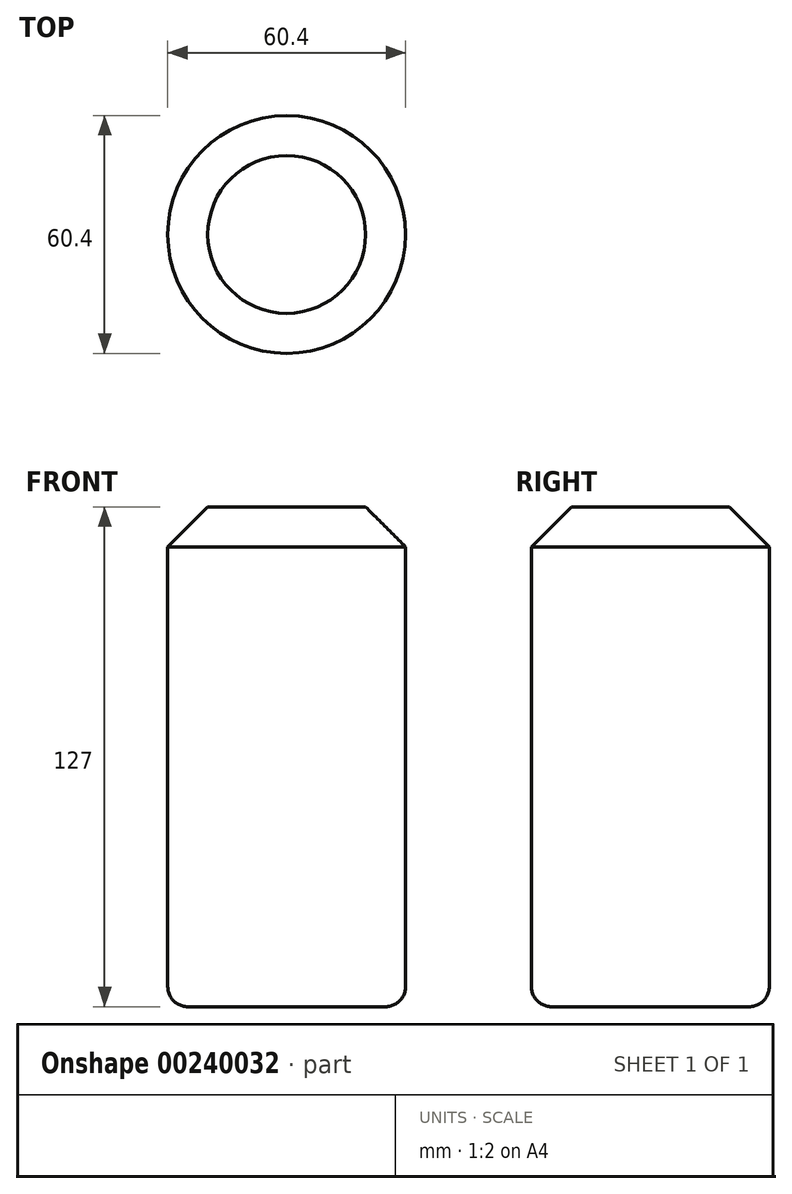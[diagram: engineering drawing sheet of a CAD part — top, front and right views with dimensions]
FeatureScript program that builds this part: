
annotation { "Feature Type Name" : "Feature", "Feature Type Description" : "" }
export const myFeature = defineFeature(function(context is Context, id is Id, definition is map)
    precondition{}
    {
        {
            var Q0;
            Q0=qCreatedBy(makeId("Top.planeOp"),FACE);
            var sketch = newSketch(context, id + "F0", { "sketchPlane" : qUnion([Q0])});
            skCircle(sketch, "E0", {"center": v(0, 0) * mm, "radius": 30.2 * mm});
            skSolve(sketch);
        }
        {
            var Q0;
            Q0=makeQuery(id+"F0.imprint","IMPRINT",FACE,{"disambiguationData":[TD([[makeQuery(id+"F0.imprint","IMPRINT",EDGE,{"derivedFrom":sQuery(id+"F0.wireOp",EDGE,"E0")}),1.0]])]});
            extrude(context, id + "F1", {"entities" : qUnion([Q0]), "depth" : 127 * mm});
        }
        {
            var Q0;
            Q0=makeQuery(id+"F1.opExtrude","CAP_FACE",FACE,{"disambiguationData":[OSD([sQuery(id+"F0.wireOp",EDGE,"E0")])],"isStart":true});
            fillet(context, id + "F2", {"entities" : qUnion([Q0]), "radius" : 5.08 * mm, "tangentPropagation" : true, "allowEdgeOverflow" : false});
        }
        {
            var Q0;
            Q0=makeQuery(id+"F1.opExtrude","CAP_FACE",FACE,{"disambiguationData":[OSD([sQuery(id+"F0.wireOp",EDGE,"E0")])],"isStart":false});
            chamfer(context, id + "F3", {"entities" : qUnion([Q0]), "width" : 10.16 * mm, "tangentPropagation" : true});
        }
    });
